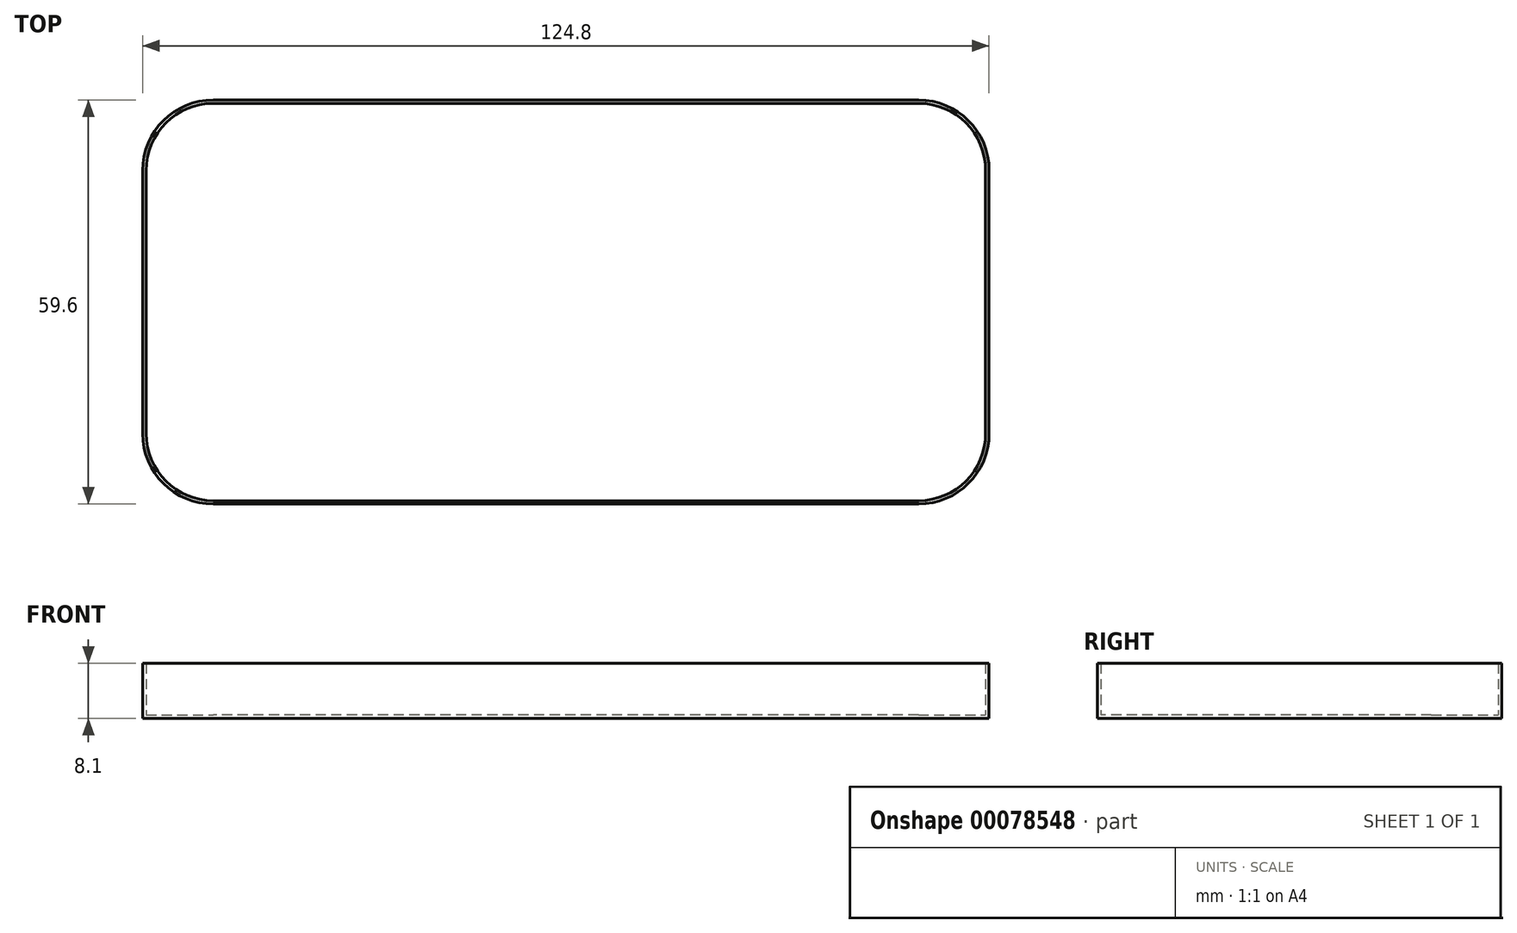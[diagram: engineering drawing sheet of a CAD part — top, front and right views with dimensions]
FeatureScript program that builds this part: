
annotation { "Feature Type Name" : "Feature", "Feature Type Description" : "" }
export const myFeature = defineFeature(function(context is Context, id is Id, definition is map)
    precondition{}
    {
        {
            var Q0;
            Q0=qCreatedBy(makeId("Top.planeOp"),FACE);
            var sketch = newSketch(context, id + "F0", { "sketchPlane" : qUnion([Q0])});
            skLineSegment(sketch, "E0.bottom", {"start": v(0, 0) * mm, "end": v(-124.8, 0) * mm});
            skLineSegment(sketch, "E0.top", {"start": v(0, -59.6) * mm, "end": v(-124.8, -59.6) * mm});
            skLineSegment(sketch, "E0.left", {"start": v(0, 0) * mm, "end": v(0, -59.6) * mm});
            skLineSegment(sketch, "E0.right", {"start": v(-124.8, 0) * mm, "end": v(-124.8, -59.6) * mm});
            skSolve(sketch);
        }
        {
            var Q0;
            Q0=makeQuery(id+"F0.imprint","IMPRINT",FACE,{"disambiguationData":[TD([[makeQuery(id+"F0.imprint","IMPRINT",EDGE,{"derivedFrom":sQuery(id+"F0.wireOp",EDGE,"E0.bottom")}),1.0]])]});
            extrude(context, id + "F1", {"entities" : qUnion([Q0]), "depth" : 8.1 * mm});
        }
        {
            var Q0;
            Q0=makeQuery(id+"F1.opExtrude","SWEPT_EDGE",EDGE,{"disambiguationData":[OSD([sQuery(id+"F0.wireOp",EDGE,"E0.top"),sQuery(id+"F0.wireOp",EDGE,"E0.left")])]});
            fillet(context, id + "F2", {"entities" : qUnion([Q0]), "radius" : 10.4 * mm, "tangentPropagation" : true, "allowEdgeOverflow" : false});
        }
        {
            var Q0;
            Q0=makeQuery(id+"F1.opExtrude","SWEPT_EDGE",EDGE,{"disambiguationData":[OSD([sQuery(id+"F0.wireOp",EDGE,"E0.bottom"),sQuery(id+"F0.wireOp",EDGE,"E0.left")])]});
            var Q1;
            Q1=makeQuery(id+"F1.opExtrude","SWEPT_EDGE",EDGE,{"disambiguationData":[OSD([sQuery(id+"F0.wireOp",EDGE,"E0.top"),sQuery(id+"F0.wireOp",EDGE,"E0.right")])]});
            var Q2;
            Q2=makeQuery(id+"F1.opExtrude","SWEPT_EDGE",EDGE,{"disambiguationData":[OSD([sQuery(id+"F0.wireOp",EDGE,"E0.bottom"),sQuery(id+"F0.wireOp",EDGE,"E0.right")])]});
            fillet(context, id + "F3", {"entities" : qUnion([Q0, Q1, Q2]), "radius" : 10.4 * mm, "tangentPropagation" : true, "allowEdgeOverflow" : false});
        }
        {
            var Q0;
            Q0=makeQuery(id+"F1.opExtrude","CAP_FACE",FACE,{"disambiguationData":[OSD([sQuery(id+"F0.wireOp",EDGE,"E0.bottom"),sQuery(id+"F0.wireOp",EDGE,"E0.top"),sQuery(id+"F0.wireOp",EDGE,"E0.left"),sQuery(id+"F0.wireOp",EDGE,"E0.right")])],"isStart":false});
            shell(context, id + "F4", {"entities" : qUnion([Q0]), "thickness" : 0.5 * mm});
        }
    });
